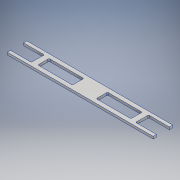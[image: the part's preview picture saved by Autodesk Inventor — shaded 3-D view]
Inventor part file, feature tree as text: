
AUTODESK INVENTOR PART (.ipt)
format: ipt  version: 2017 (Build 210142000, 142)  size: 141,824 bytes
history: native  units: mm
features: extrude x1, sketch x1
ambient origin geometry x8: Origin, YZ Plane, XZ Plane, XY Plane, X Axis, Y Axis, Z Axis, Center Point
bodies: Body1 (feature_tree)
feature tree (2):
  extrude  "Extrusion2"  Depth=50.8mm
  sketch  "Sketch1"  dims[d0=135.4mm d1=44.0mm d8=78.105mm d13=50.8mm d14=44.45mm d15=21.59mm d18=135.4mm d19=44.0mm d20=78.105mm d21=50.8mm d26=568.96mm d33=21.59mm d36=9.525mm d37=0.0mm]
